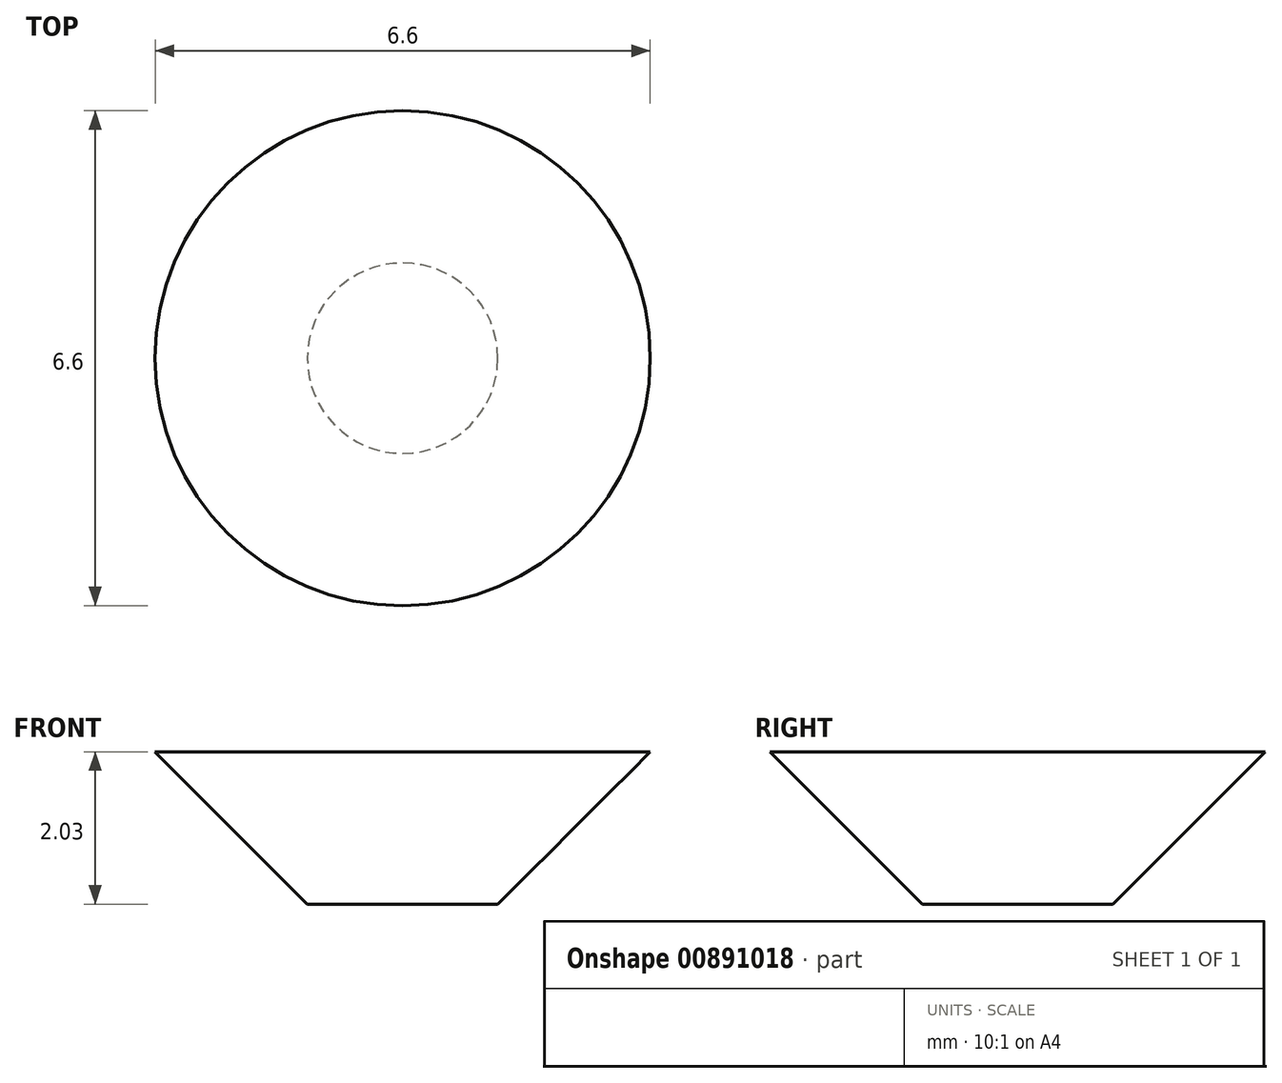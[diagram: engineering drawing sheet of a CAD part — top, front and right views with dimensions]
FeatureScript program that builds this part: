
annotation { "Feature Type Name" : "Feature", "Feature Type Description" : "" }
export const myFeature = defineFeature(function(context is Context, id is Id, definition is map)
    precondition{}
    {
        {
            var Q0;
            Q0=qCreatedBy(makeId("Top.planeOp"),FACE);
            var sketch = newSketch(context, id + "F0", { "sketchPlane" : qUnion([Q0])});
            skCircle(sketch, "E0", {"center": v(0, 0) * mm, "radius": 3.81 * mm});
            skSolve(sketch);
        }
        {
            var Q0;
            Q0 = qSketchRegion(id + "F0", true);
            extrude(context, id + "F1", {"entities" : qUnion([Q0]), "oppositeDirection" : true, "depth" : 2.03 * mm, "offsetDistance" : 25.4 * mm});
        }
        {
            var Q0;
            Q0=makeQuery(id+"F1.opExtrude","CAP_FACE",FACE,{"disambiguationData":[OSD([sQuery(id+"F0.wireOp",EDGE,"E0")])],"isStart":false});
            chamfer(context, id + "F2", {"entities" : qUnion([Q0]), "width" : 2.54 * mm, "tangentPropagation" : true});
        }
    });
